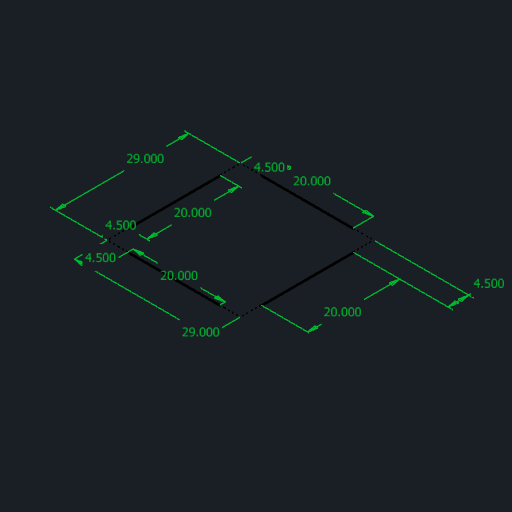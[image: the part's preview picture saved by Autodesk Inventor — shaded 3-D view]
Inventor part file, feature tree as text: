
AUTODESK INVENTOR PART (.ipt)
format: ipt  version: 2022.2 (Build 262287000, 287)  size: 76,288 bytes
history: native  units: mm (DEFAULTED — no unit token found)
features: sketch x1
ambient origin geometry x8: Origin, YZ Plane, XZ Plane, XY Plane, X Axis, Y Axis, Z Axis, Center Point
feature tree (1):
  sketch  "Sketch1"  dims[d0=736.6mm d1=736.6mm d2=508.0mm d3=114.3mm d4=508.0mm d5=114.3mm d6=114.3mm d7=508.0mm d8=508.0mm d9=114.3mm]
